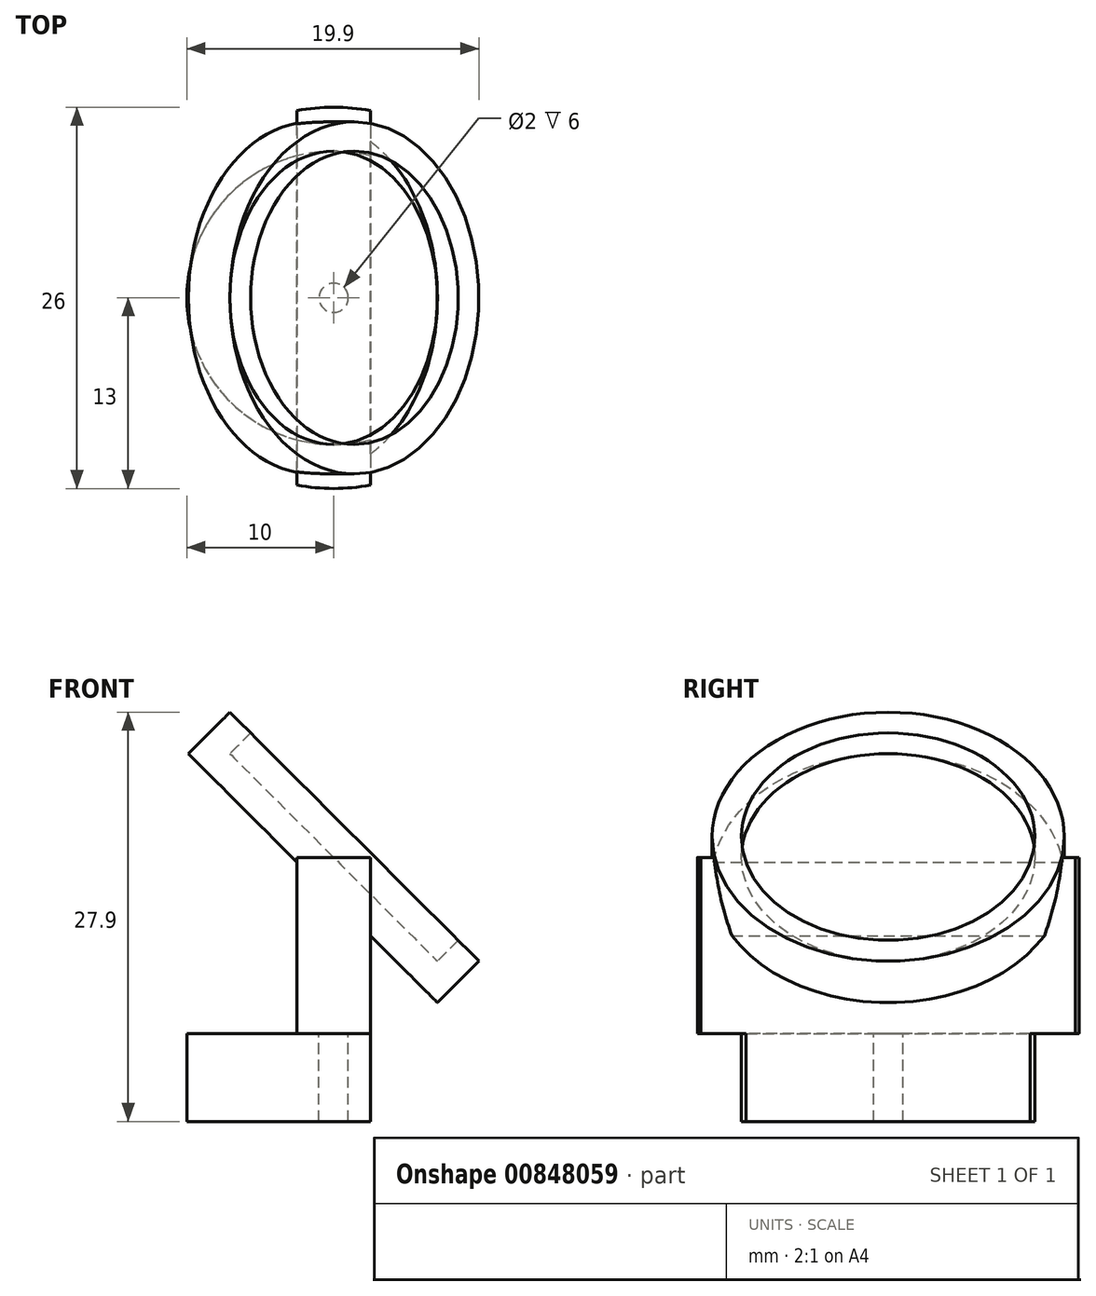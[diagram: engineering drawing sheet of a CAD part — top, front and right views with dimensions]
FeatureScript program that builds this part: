
annotation { "Feature Type Name" : "Feature", "Feature Type Description" : "" }
export const myFeature = defineFeature(function(context is Context, id is Id, definition is map)
    precondition{}
    {
        {
            var Q0;
            Q0=qCreatedBy(makeId("Top.planeOp"),FACE);
            var sketch = newSketch(context, id + "F0", { "sketchPlane" : qUnion([Q0])});
            skCircle(sketch, "E0", {"center": v(0, 0) * mm, "radius": 13 * mm});
            skLineSegment(sketch, "E1", {"start": v(-13, 0) * mm, "end": v(13, 0) * mm});
            skLineSegment(sketch, "E2", {"start": v(0, -13) * mm, "end": v(0, 13) * mm});
            skLineSegment(sketch, "E3.bottom", {"start": v(-2.5, 13) * mm, "end": v(2.5, 13) * mm});
            skLineSegment(sketch, "E3.top", {"start": v(-2.5, -13) * mm, "end": v(2.5, -13) * mm});
            skLineSegment(sketch, "E3.left", {"start": v(-2.5, 13) * mm, "end": v(-2.5, -13) * mm});
            skLineSegment(sketch, "E3.right", {"start": v(2.5, 13) * mm, "end": v(2.5, -13) * mm});
            skSolve(sketch);
        }
        {
            var Q0;
            Q0=qCreatedBy(makeId("Front.planeOp"),FACE);
            var sketch = newSketch(context, id + "F1", { "sketchPlane" : qUnion([Q0])});
            skLineSegment(sketch, "E4", {"start": v(0, 0) * mm, "end": v(-28.35, 28.35) * mm});
            skSolve(sketch);
        }
        {
            var Q0;
            Q0=sQuery(id+"F0.wireOp",VERTEX,"E2.start");
            var Q1;
            Q1=sQuery(id+"F0.wireOp",VERTEX,"E0.center");
            var Q2;
            Q2=sQuery(id+"F1.wireOp",VERTEX,"E4.end");
            cPlane(context, id + "F2", {"entities" : qUnion([Q0, Q1, Q2]), "cplaneType" : CPlaneType.THREE_POINT, "offset" : 25 * mm, "width" : 150 * mm, "height" : 150 * mm});
        }
        {
            var Q0;
            Q0=qCreatedBy(id+"F2.planeOp",FACE);
            var sketch = newSketch(context, id + "F3", { "sketchPlane" : qUnion([Q0])});
            skCircle(sketch, "E5", {"center": v(0, 0) * mm, "radius": 12 * mm});
            skCircle(sketch, "E6", {"center": v(0, 0) * mm, "radius": 10 * mm});
            skSolve(sketch);
        }
        {
            var Q0;
            Q0=makeQuery(id+"F3.imprint","IMPRINT",FACE,{"disambiguationData":[TD([[makeQuery(id+"F3.imprint","IMPRINT",EDGE,{"derivedFrom":sQuery(id+"F3.wireOp",EDGE,"E5")}),1.0]])]});
            var Q1;
            Q1=makeQuery(id+"F3.imprint","IMPRINT",FACE,{"disambiguationData":[TD([[makeQuery(id+"F3.imprint","IMPRINT",EDGE,{"derivedFrom":sQuery(id+"F3.wireOp",EDGE,"E6")}),1.0]])]});
            extrude(context, id + "F4", {"entities" : qUnion([Q0, Q1]), "endBound" : BoundingType.SYMMETRIC, "oppositeDirection" : true, "depth" : 4 * mm, "offsetDistance" : 25 * mm});
        }
        {
            var Q0;
            {var subQ3=sQuery(id+"F0.wireOp",EDGE,"E3.left");var subQ5=sQuery(id+"F0.wireOp",EDGE,"E1");var subQ6=makeQuery(id+"F0.imprint","INTERSECT",VERTEX,{"derivedFrom":[subQ5,subQ3]});Q0=makeQuery(id+"F0.imprint","IMPRINT",FACE,{"disambiguationData":[TD([[makeQuery(id+"F0.imprint","IMPRINT",EDGE,{"disambiguationData":[TD([[subQ6,-1.0]])],"derivedFrom":subQ5}),-1.0]])]});}
            var Q1;
            {var subQ3=sQuery(id+"F0.wireOp",EDGE,"E3.left");var subQ5=sQuery(id+"F0.wireOp",EDGE,"E1");var subQ6=makeQuery(id+"F0.imprint","INTERSECT",VERTEX,{"derivedFrom":[subQ5,subQ3]});Q1=makeQuery(id+"F0.imprint","IMPRINT",FACE,{"disambiguationData":[TD([[makeQuery(id+"F0.imprint","IMPRINT",EDGE,{"disambiguationData":[TD([[subQ6,-1.0]])],"derivedFrom":subQ5}),1.0]])]});}
            var Q2;
            {var subQ0=sQuery(id+"F0.wireOp",EDGE,"E2");var subQ5=sQuery(id+"F0.wireOp",EDGE,"E1");var subQ6=makeQuery(id+"F0.imprint","INTERSECT",VERTEX,{"derivedFrom":[subQ5,subQ0]});Q2=makeQuery(id+"F0.imprint","IMPRINT",FACE,{"disambiguationData":[TD([[makeQuery(id+"F0.imprint","IMPRINT",EDGE,{"disambiguationData":[TD([[subQ6,-1.0]])],"derivedFrom":subQ5}),1.0]])]});}
            var Q3;
            {var subQ0=sQuery(id+"F0.wireOp",EDGE,"E2");var subQ5=sQuery(id+"F0.wireOp",EDGE,"E1");var subQ6=makeQuery(id+"F0.imprint","INTERSECT",VERTEX,{"derivedFrom":[subQ5,subQ0]});Q3=makeQuery(id+"F0.imprint","IMPRINT",FACE,{"disambiguationData":[TD([[makeQuery(id+"F0.imprint","IMPRINT",EDGE,{"disambiguationData":[TD([[subQ6,-1.0]])],"derivedFrom":subQ5}),-1.0]])]});}
            extrude(context, id + "F5", {"entities" : qUnion([Q0, Q1, Q2, Q3]), "operationType" : NewBodyOperationType.ADD, "oppositeDirection" : true, "depth" : 12 * mm, "offsetDistance" : 25 * mm});
        }
        {
            var Q0;
            Q0=makeQuery(id+"F5.opExtrude","CAP_FACE",FACE,{"disambiguationData":[OSD([sQuery(id+"F0.wireOp",EDGE,"E0"),sQuery(id+"F0.wireOp",EDGE,"E3.left"),sQuery(id+"F0.wireOp",EDGE,"E3.right")])],"isStart":false});
            var sketch = newSketch(context, id + "F6", { "sketchPlane" : qUnion([Q0])});
            skCircle(sketch, "E7", {"center": v(0, 0) * mm, "radius": 10 * mm});
            skCircle(sketch, "E8", {"center": v(0, 0) * mm, "radius": 1 * mm});
            skSolve(sketch);
        }
        {
            var Q0;
            {var subQ0=sQuery(id+"F6.wireOp",EDGE,"E7");var subQ1=makeQuery(id+"F5.opExtrude","CAP_EDGE",EDGE,{"disambiguationData":[OSD([sQuery(id+"F0.wireOp",EDGE,"E3.right")])],"isStart":false});var subQ2=makeQuery(id+"F6.imprint","INTERSECT",VERTEX,{"disambiguationData":[OD(0.0)],"derivedFrom":[subQ1,subQ0]});Q0=makeQuery(id+"F6.imprint","IMPRINT",FACE,{"disambiguationData":[TD([[makeQuery(id+"F6.imprint","IMPRINT",EDGE,{"disambiguationData":[TD([[subQ2,1.0]])],"derivedFrom":subQ0}),1.0]])]});}
            var Q1;
            {var subQ0=sQuery(id+"F6.wireOp",EDGE,"E7");var subQ1=makeQuery(id+"F5.opExtrude","CAP_EDGE",EDGE,{"disambiguationData":[OSD([sQuery(id+"F0.wireOp",EDGE,"E3.left")])],"isStart":false});var subQ2=makeQuery(id+"F6.imprint","INTERSECT",VERTEX,{"disambiguationData":[OD(0.0)],"derivedFrom":[subQ1,subQ0]});Q1=makeQuery(id+"F6.imprint","IMPRINT",FACE,{"disambiguationData":[TD([[makeQuery(id+"F6.imprint","IMPRINT",EDGE,{"disambiguationData":[TD([[subQ2,-1.0]])],"derivedFrom":subQ0}),1.0]])]});}
            var Q2;
            {var subQ0=sQuery(id+"F6.wireOp",EDGE,"E7");var subQ1=makeQuery(id+"F5.opExtrude","CAP_EDGE",EDGE,{"disambiguationData":[OSD([sQuery(id+"F0.wireOp",EDGE,"E3.left")])],"isStart":false});var subQ2=makeQuery(id+"F6.imprint","INTERSECT",VERTEX,{"disambiguationData":[OD(0.0)],"derivedFrom":[subQ1,subQ0]});Q2=makeQuery(id+"F6.imprint","IMPRINT",FACE,{"disambiguationData":[TD([[makeQuery(id+"F6.imprint","IMPRINT",EDGE,{"disambiguationData":[TD([[subQ2,1.0]])],"derivedFrom":subQ0}),1.0]])]});}
            extrude(context, id + "F7", {"entities" : qUnion([Q0, Q1, Q2]), "operationType" : NewBodyOperationType.ADD, "depth" : 6 * mm, "offsetDistance" : 25 * mm});
        }
        {
            var Q0;
            Q0=makeQuery(id+"F3.imprint","IMPRINT",FACE,{"disambiguationData":[TD([[makeQuery(id+"F3.imprint","IMPRINT",EDGE,{"derivedFrom":sQuery(id+"F3.wireOp",EDGE,"E6")}),1.0]])]});
            extrude(context, id + "F8", {"entities" : qUnion([Q0]), "operationType" : NewBodyOperationType.REMOVE, "oppositeDirection" : true, "depth" : 2 * mm, "offsetDistance" : 25 * mm});
        }
    });
